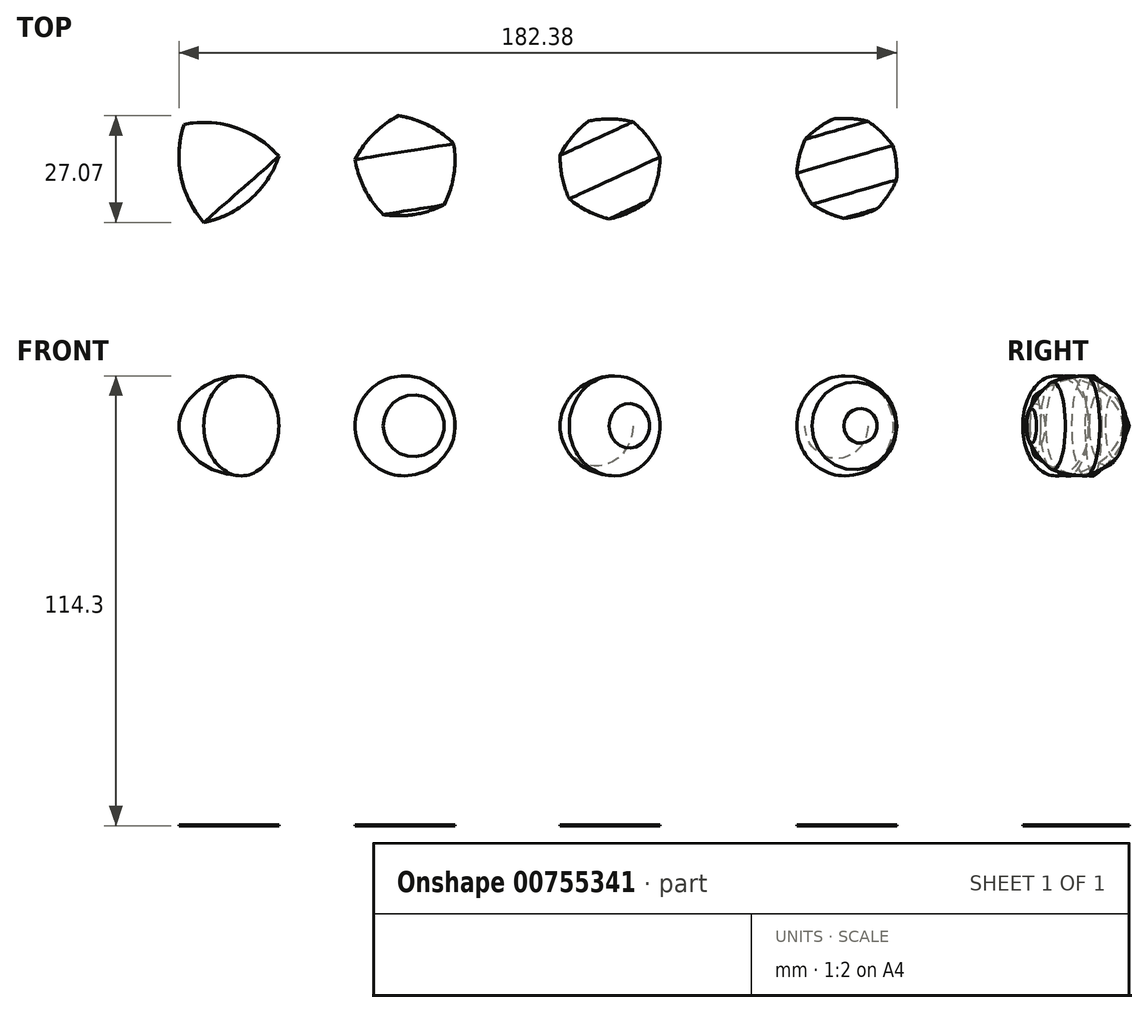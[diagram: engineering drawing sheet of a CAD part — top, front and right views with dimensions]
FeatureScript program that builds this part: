
annotation { "Feature Type Name" : "Feature", "Feature Type Description" : "" }
export const myFeature = defineFeature(function(context is Context, id is Id, definition is map)
    precondition{}
    {
        {
            assignVariable(context, id + "F0", {"name" : "Height", "anyValue" : .25});
        }
        {
            var Q0;
            Q0=qCreatedBy(makeId("Top.planeOp"),FACE);
            var sketch = newSketch(context, id + "F1", { "sketchPlane" : qUnion([Q0])});
            skCircle(sketch, "E0.cCircle", {"center": v(0, 0) * mm, "radius": 7.33 * mm, "construction": true});
            skLineSegment(sketch, "E0.0", {"start": v(-4.7, -13.9) * mm, "end": v(-9.69, 11) * mm, "construction": true});
            skLineSegment(sketch, "E0.1", {"start": v(-9.69, 11) * mm, "end": v(14.38, 2.88) * mm, "construction": true});
            skLineSegment(sketch, "E0.2", {"start": v(14.38, 2.88) * mm, "end": v(-4.7, -13.9) * mm, "construction": true});
            skPoint(sketch, "E0.0.midPoint", {"position": v(-7.19, -1.44) * mm});
            skArc(sketch, "E1", {"start": v(-9.69, 11) * mm, "mid": v(3.43, 10.17) * mm, "end": v(14.38, 2.88) * mm});
            skArc(sketch, "E2", {"start": v(14.38, 2.88) * mm, "mid": v(7.1, -8.06) * mm, "end": v(-4.7, -13.9) * mm});
            skArc(sketch, "E3", {"start": v(-4.7, -13.9) * mm, "mid": v(-10.53, -2.11) * mm, "end": v(-9.69, 11) * mm});
            skLineSegment(sketch, "E4", {"start": v(0, 0) * mm, "end": v(257.11, 0) * mm, "construction": true});
            skCircle(sketch, "E5.cCircle", {"center": v(46.93, 0) * mm, "radius": 10.8 * mm, "construction": true});
            skLineSegment(sketch, "E5.0", {"start": v(33.73, 2.05) * mm, "end": v(44.8, 13.18) * mm, "construction": true});
            skLineSegment(sketch, "E5.1", {"start": v(44.8, 13.18) * mm, "end": v(58.8, 6.1) * mm, "construction": true});
            skLineSegment(sketch, "E5.2", {"start": v(58.8, 6.1) * mm, "end": v(56.4, -9.42) * mm, "construction": true});
            skLineSegment(sketch, "E5.3", {"start": v(56.4, -9.42) * mm, "end": v(40.9, -11.91) * mm, "construction": true});
            skLineSegment(sketch, "E5.4", {"start": v(40.9, -11.91) * mm, "end": v(33.73, 2.05) * mm, "construction": true});
            skPoint(sketch, "E5.0.midPoint", {"position": v(39.27, 7.62) * mm});
            skCircle(sketch, "E6.cCircle", {"center": v(98.47, 0) * mm, "radius": 11.74 * mm, "construction": true});
            skLineSegment(sketch, "E6.0", {"start": v(85.82, 3.1) * mm, "end": v(93, 11.82) * mm, "construction": true});
            skLineSegment(sketch, "E6.1", {"start": v(93, 11.82) * mm, "end": v(104.3, 11.65) * mm, "construction": true});
            skLineSegment(sketch, "E6.2", {"start": v(104.3, 11.65) * mm, "end": v(111.21, 2.7) * mm, "construction": true});
            skLineSegment(sketch, "E6.3", {"start": v(111.21, 2.7) * mm, "end": v(108.53, -8.28) * mm, "construction": true});
            skLineSegment(sketch, "E6.4", {"start": v(108.53, -8.28) * mm, "end": v(98.27, -13.03) * mm, "construction": true});
            skLineSegment(sketch, "E6.5", {"start": v(98.27, -13.03) * mm, "end": v(88.16, -7.96) * mm, "construction": true});
            skLineSegment(sketch, "E6.6", {"start": v(88.16, -7.96) * mm, "end": v(85.82, 3.1) * mm, "construction": true});
            skPoint(sketch, "E6.0.midPoint", {"position": v(89.4, 7.46) * mm});
            skCircle(sketch, "E7.cCircle", {"center": v(158.78, 0) * mm, "radius": 12.12 * mm, "construction": true});
            skLineSegment(sketch, "E7.0", {"start": v(164, 11.79) * mm, "end": v(170.36, 5.67) * mm, "construction": true});
            skLineSegment(sketch, "E7.1", {"start": v(170.36, 5.67) * mm, "end": v(171.3, -3.1) * mm, "construction": true});
            skLineSegment(sketch, "E7.2", {"start": v(171.3, -3.1) * mm, "end": v(166.38, -10.42) * mm, "construction": true});
            skLineSegment(sketch, "E7.3", {"start": v(166.38, -10.42) * mm, "end": v(157.9, -12.87) * mm, "construction": true});
            skLineSegment(sketch, "E7.4", {"start": v(157.9, -12.87) * mm, "end": v(149.84, -9.29) * mm, "construction": true});
            skLineSegment(sketch, "E7.5", {"start": v(149.84, -9.29) * mm, "end": v(145.96, -1.37) * mm, "construction": true});
            skLineSegment(sketch, "E7.6", {"start": v(145.96, -1.37) * mm, "end": v(148.08, 7.2) * mm, "construction": true});
            skLineSegment(sketch, "E7.7", {"start": v(148.08, 7.2) * mm, "end": v(155.2, 12.4) * mm, "construction": true});
            skLineSegment(sketch, "E7.8", {"start": v(155.2, 12.4) * mm, "end": v(164, 11.79) * mm, "construction": true});
            skPoint(sketch, "E7.0.midPoint", {"position": v(167.19, 8.73) * mm});
            skArc(sketch, "E8", {"start": v(33.73, 2.05) * mm, "mid": v(38.39, 8.5) * mm, "end": v(44.8, 13.18) * mm});
            skArc(sketch, "E9", {"start": v(44.8, 13.18) * mm, "mid": v(52.37, 10.75) * mm, "end": v(58.8, 6.1) * mm});
            skArc(sketch, "E10", {"start": v(58.8, 6.1) * mm, "mid": v(58.83, -1.85) * mm, "end": v(56.4, -9.42) * mm});
            skArc(sketch, "E11", {"start": v(56.4, -9.42) * mm, "mid": v(48.84, -11.9) * mm, "end": v(40.9, -11.91) * mm});
            skArc(sketch, "E12", {"start": v(40.9, -11.91) * mm, "mid": v(36.2, -5.5) * mm, "end": v(33.73, 2.05) * mm});
            skArc(sketch, "E13", {"start": v(93, 11.82) * mm, "mid": v(98.66, 12.37) * mm, "end": v(104.3, 11.65) * mm});
            skArc(sketch, "E14", {"start": v(85.82, 3.1) * mm, "mid": v(88.92, 7.87) * mm, "end": v(93, 11.82) * mm});
            skArc(sketch, "E15", {"start": v(88.16, -7.96) * mm, "mid": v(86.37, -2.56) * mm, "end": v(85.82, 3.1) * mm});
            skArc(sketch, "E16", {"start": v(98.27, -13.03) * mm, "mid": v(92.93, -11.06) * mm, "end": v(88.16, -7.96) * mm});
            skArc(sketch, "E17", {"start": v(108.53, -8.28) * mm, "mid": v(103.66, -11.23) * mm, "end": v(98.27, -13.03) * mm});
            skArc(sketch, "E18", {"start": v(111.21, 2.7) * mm, "mid": v(110.49, -2.94) * mm, "end": v(108.53, -8.28) * mm});
            skArc(sketch, "E19", {"start": v(104.3, 11.65) * mm, "mid": v(108.26, 7.56) * mm, "end": v(111.21, 2.7) * mm});
            skArc(sketch, "E20", {"start": v(155.2, 12.4) * mm, "mid": v(159.64, 12.47) * mm, "end": v(164, 11.79) * mm});
            skArc(sketch, "E21", {"start": v(148.08, 7.2) * mm, "mid": v(151.42, 10.1) * mm, "end": v(155.2, 12.4) * mm});
            skArc(sketch, "E22", {"start": v(145.96, -1.37) * mm, "mid": v(146.64, 3) * mm, "end": v(148.08, 7.2) * mm});
            skArc(sketch, "E23", {"start": v(149.84, -9.29) * mm, "mid": v(147.55, -5.5) * mm, "end": v(145.96, -1.37) * mm});
            skArc(sketch, "E24", {"start": v(157.9, -12.87) * mm, "mid": v(153.71, -11.43) * mm, "end": v(149.84, -9.29) * mm});
            skArc(sketch, "E25", {"start": v(166.38, -10.42) * mm, "mid": v(162.25, -12.01) * mm, "end": v(157.9, -12.87) * mm});
            skArc(sketch, "E26", {"start": v(171.3, -3.1) * mm, "mid": v(169.16, -6.98) * mm, "end": v(166.38, -10.42) * mm});
            skArc(sketch, "E27", {"start": v(170.36, 5.67) * mm, "mid": v(171.22, 1.33) * mm, "end": v(171.3, -3.1) * mm});
            skArc(sketch, "E28", {"start": v(164, 11.79) * mm, "mid": v(167.45, 9) * mm, "end": v(170.36, 5.67) * mm});
            skSolve(sketch);
        }
        {
            var Q0;
            Q0 = qSketchRegion(id + "F1", true);
            extrude(context, id + "F2", {"entities" : qUnion([Q0]), "depth" : (getVariable(context, 'Height')) * mm, "offsetDistance" : 25.4 * mm});
        }
        {
            var Q0;
            Q0=qCreatedBy(makeId("Top.planeOp"),FACE);
            cPlane(context, id + "F3", {"entities" : qUnion([Q0]), "cplaneType" : CPlaneType.OFFSET, "offset" : 101.6 * mm, "width" : 152.4 * mm, "height" : 152.4 * mm});
        }
        {
            var Q0;
            Q0=qCreatedBy(id+"F3.planeOp",FACE);
            var sketch = newSketch(context, id + "F4", { "sketchPlane" : qUnion([Q0])});
            skArc(sketch, "E29.0.0", {"start": v(-9.69, 11) * mm, "mid": v(-10.53, -2.11) * mm, "end": v(-4.7, -13.9) * mm});
            skArc(sketch, "E29.0.1", {"start": v(-4.7, -13.9) * mm, "mid": v(7.1, -8.06) * mm, "end": v(14.38, 2.88) * mm, "construction": true});
            skArc(sketch, "E29.1.0", {"start": v(33.73, 2.05) * mm, "mid": v(36.2, -5.5) * mm, "end": v(40.9, -11.91) * mm});
            skArc(sketch, "E29.1.1", {"start": v(40.9, -11.91) * mm, "mid": v(48.84, -11.9) * mm, "end": v(56.4, -9.42) * mm, "construction": true});
            skArc(sketch, "E29.1.4", {"start": v(44.8, 13.18) * mm, "mid": v(38.39, 8.5) * mm, "end": v(33.73, 2.05) * mm});
            skArc(sketch, "E29.2.2", {"start": v(93, 11.82) * mm, "mid": v(88.92, 7.87) * mm, "end": v(85.82, 3.1) * mm});
            skArc(sketch, "E29.2.3", {"start": v(85.82, 3.1) * mm, "mid": v(86.37, -2.56) * mm, "end": v(88.16, -7.96) * mm});
            skArc(sketch, "E29.2.4", {"start": v(88.16, -7.96) * mm, "mid": v(92.93, -11.06) * mm, "end": v(98.27, -13.03) * mm});
            skArc(sketch, "E29.2.5", {"start": v(98.27, -13.03) * mm, "mid": v(103.66, -11.23) * mm, "end": v(108.53, -8.28) * mm, "construction": true});
            skArc(sketch, "E29.3.2", {"start": v(155.2, 12.4) * mm, "mid": v(151.42, 10.1) * mm, "end": v(148.08, 7.2) * mm});
            skArc(sketch, "E29.3.3", {"start": v(148.08, 7.2) * mm, "mid": v(146.64, 3) * mm, "end": v(145.96, -1.37) * mm});
            skArc(sketch, "E29.3.4", {"start": v(145.96, -1.37) * mm, "mid": v(147.55, -5.5) * mm, "end": v(149.84, -9.29) * mm});
            skArc(sketch, "E29.3.5", {"start": v(149.84, -9.29) * mm, "mid": v(153.71, -11.43) * mm, "end": v(157.9, -12.87) * mm});
            skArc(sketch, "E29.3.6", {"start": v(157.9, -12.87) * mm, "mid": v(160.1, -12.54) * mm, "end": v(162.25, -12.01) * mm});
            skLineSegment(sketch, "E30", {"start": v(-9.69, 11) * mm, "end": v(7.1, -8.06) * mm});
            skLineSegment(sketch, "E31", {"start": v(44.8, 13.18) * mm, "end": v(48.84, -11.9) * mm});
            skLineSegment(sketch, "E32", {"start": v(93, 11.82) * mm, "end": v(103.66, -11.23) * mm});
            skLineSegment(sketch, "E33", {"start": v(155.2, 12.4) * mm, "end": v(162.25, -12.01) * mm});
            skPoint(sketch, "E29.1.2.end.orphan", {"position": v(58.8, 6.1) * mm});
            skPoint(sketch, "E29.2.0.end.orphan", {"position": v(104.3, 11.65) * mm});
            skPoint(sketch, "E29.2.6.end.orphan", {"position": v(111.21, 2.7) * mm});
            skPoint(sketch, "E29.3.0.end.orphan", {"position": v(164, 11.79) * mm});
            skPoint(sketch, "E29.3.8.end.orphan", {"position": v(170.36, 5.67) * mm});
            skPoint(sketch, "E29.3.7.end.orphan", {"position": v(171.3, -3.1) * mm});
            skArc(sketch, "E34.0", {"start": v(7.1, -8.06) * mm, "mid": v(1.58, -11.75) * mm, "end": v(-4.7, -13.9) * mm});
            skArc(sketch, "E34.1", {"start": v(48.84, -11.9) * mm, "mid": v(44.87, -12.22) * mm, "end": v(40.9, -11.91) * mm});
            skArc(sketch, "E34.2", {"start": v(103.66, -11.23) * mm, "mid": v(101.02, -12.28) * mm, "end": v(98.27, -13.03) * mm});
            skArc(sketch, "E34.3", {"start": v(166.38, -10.42) * mm, "mid": v(162.25, -12.01) * mm, "end": v(157.9, -12.87) * mm, "construction": true});
            skSolve(sketch);
        }
        {
            var Q0;
            Q0=makeQuery(id+"F4.imprint","IMPRINT",FACE,{"disambiguationData":[TD([[makeQuery(id+"F4.imprint","IMPRINT",EDGE,{"derivedFrom":sQuery(id+"F4.wireOp",EDGE,"E29.0.0")}),1.0]])]});
            var Q1;
            Q1=sQuery(id+"F4.wireOp",EDGE,"E30");
            revolve(context, id + "F5", {"surfaceOperationType" : NewSurfaceOperationType.NEW, "entities" : qUnion([Q0]), "axis" : qUnion([Q1]), "revolveType" : RevolveType.FULL});
        }
        {
            var Q0;
            Q0=makeQuery(id+"F4.imprint","IMPRINT",FACE,{"disambiguationData":[TD([[makeQuery(id+"F4.imprint","IMPRINT",EDGE,{"derivedFrom":sQuery(id+"F4.wireOp",EDGE,"E29.1.0")}),1.0]])]});
            var Q1;
            Q1=sQuery(id+"F4.wireOp",EDGE,"E31");
            revolve(context, id + "F6", {"surfaceOperationType" : NewSurfaceOperationType.NEW, "entities" : qUnion([Q0]), "axis" : qUnion([Q1]), "revolveType" : RevolveType.FULL});
        }
        {
            var Q0;
            Q0=makeQuery(id+"F4.imprint","IMPRINT",FACE,{"disambiguationData":[TD([[makeQuery(id+"F4.imprint","IMPRINT",EDGE,{"derivedFrom":sQuery(id+"F4.wireOp",EDGE,"E29.2.2")}),1.0]])]});
            var Q1;
            Q1=sQuery(id+"F4.wireOp",EDGE,"E32");
            revolve(context, id + "F7", {"surfaceOperationType" : NewSurfaceOperationType.NEW, "entities" : qUnion([Q0]), "axis" : qUnion([Q1]), "revolveType" : RevolveType.FULL});
        }
        {
            var Q0;
            Q0=makeQuery(id+"F4.imprint","IMPRINT",FACE,{"disambiguationData":[TD([[makeQuery(id+"F4.imprint","IMPRINT",EDGE,{"derivedFrom":sQuery(id+"F4.wireOp",EDGE,"E29.3.2")}),1.0]])]});
            var Q1;
            Q1=sQuery(id+"F4.wireOp",EDGE,"E33");
            revolve(context, id + "F8", {"surfaceOperationType" : NewSurfaceOperationType.NEW, "entities" : qUnion([Q0]), "axis" : qUnion([Q1]), "revolveType" : RevolveType.FULL});
        }
    });
